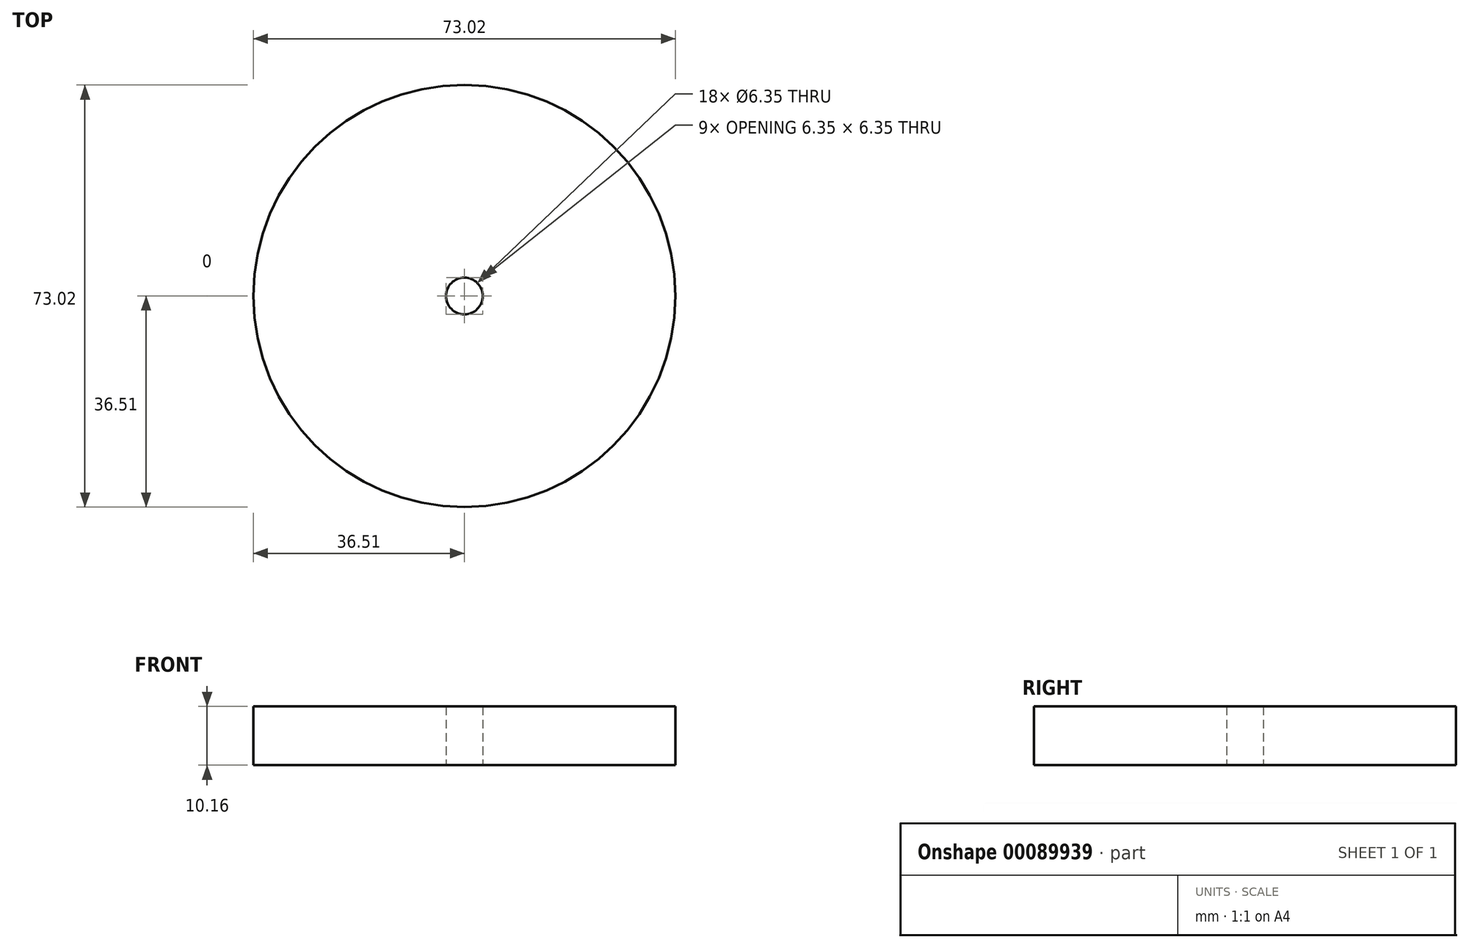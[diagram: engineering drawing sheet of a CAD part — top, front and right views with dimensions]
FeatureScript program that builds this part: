
annotation { "Feature Type Name" : "Feature", "Feature Type Description" : "" }
export const myFeature = defineFeature(function(context is Context, id is Id, definition is map)
    precondition{}
    {
        {
            var Q0;
            Q0=qCreatedBy(makeId("Top.planeOp"),FACE);
            var sketch = newSketch(context, id + "F0", { "sketchPlane" : qUnion([Q0])});
            skCircle(sketch, "E0", {"center": v(0, 0) * mm, "radius": 36.51 * mm});
            skSolve(sketch);
        }
        {
            var Q0;
            Q0 = qSketchRegion(id + "F0", true);
            extrude(context, id + "F1", {"entities" : qUnion([Q0]), "depth" : 10.16 * mm});
        }
        {
            var Q0;
            Q0=makeQuery(id+"F1.opExtrude","CAP_FACE",FACE,{"disambiguationData":[OSD([sQuery(id+"F0.wireOp",EDGE,"E0")])],"isStart":true});
            var sketch = newSketch(context, id + "F2", { "sketchPlane" : qUnion([Q0])});
            skPoint(sketch, "E1", {"position": v(0, 0) * mm});
            skSolve(sketch);
        }
        {
            var Q0;
            Q0=sQuery(id+"F2.wireOp",VERTEX,"E1");
            var Q1;
            Q1=makeQuery(id+"F1.opExtrude","SWEPT_BODY",BODY,{"disambiguationData":[OSD([sQuery(id+"F0.wireOp",EDGE,"E0")])]});
            hole(context, id + "F3", {"style" : HoleStyle.SIMPLE, "endStyle" : HoleEndStyle.THROUGH, "holeDiameter" : 6.35 * mm, "locations" : qUnion([Q0]), "scope" : qUnion([Q1]), "isTappedThrough" : true});
        }
    });
